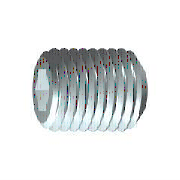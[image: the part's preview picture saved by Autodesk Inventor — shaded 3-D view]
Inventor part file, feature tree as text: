
AUTODESK INVENTOR PART (.ipt)
format: ipt  version: 2011 (Build 150239000, 239)  size: 155,648 bytes
history: native  units: mm (DEFAULTED — no unit token found)
features: extrude x1, other x1, plane x1
ambient origin geometry x8: Origin, YZ Plane, XZ Plane, XY Plane, X Axis, Y Axis, Z Axis, Center Point
bodies: Solid1 (feature_tree), Body (feature_tree)
feature tree (3):
  extrude  "Slot"  Depth=2.032mm
  other  "Work Axis1"
  plane  "Work Plane1"
